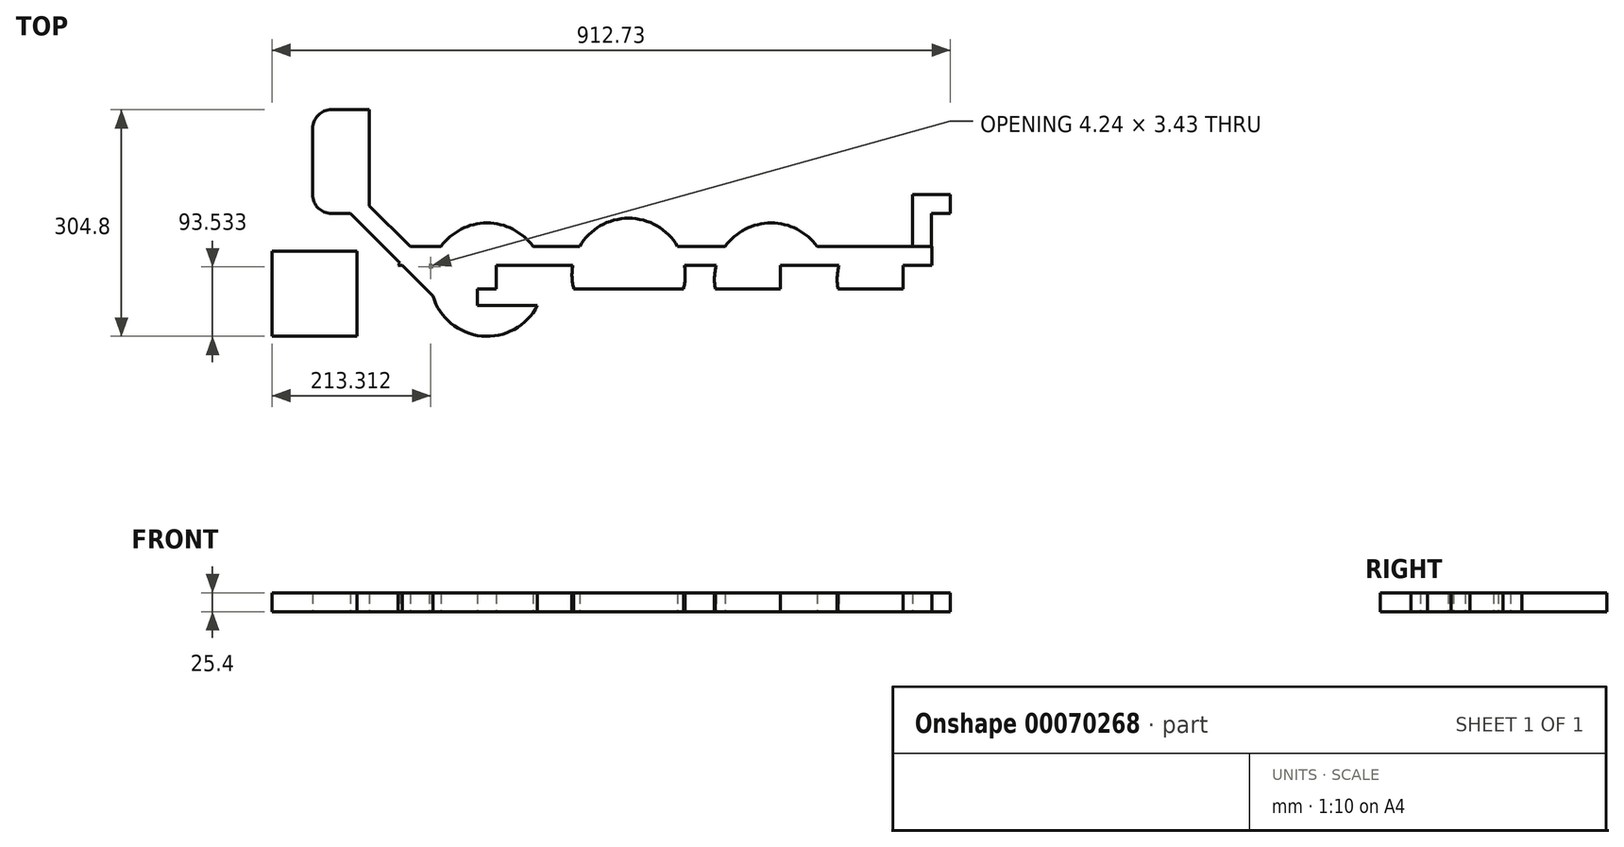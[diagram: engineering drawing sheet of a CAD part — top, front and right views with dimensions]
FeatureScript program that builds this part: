
annotation { "Feature Type Name" : "Feature", "Feature Type Description" : "" }
export const myFeature = defineFeature(function(context is Context, id is Id, definition is map)
    precondition{}
    {
        {
            var Q0;
            Q0=qCreatedBy(makeId("Top.planeOp"),FACE);
            var sketch = newSketch(context, id + "F0", { "sketchPlane" : qUnion([Q0])});
            skPoint(sketch, "E0", {"position": v(76.2, 76.2) * mm});
            skCircle(sketch, "E1", {"center": v(76.2, 76.2) * mm, "radius": 76.2 * mm});
            skLineSegment(sketch, "E2.left", {"start": v(63.5, 88.9) * mm, "end": v(63.5, 63.5) * mm});
            skLineSegment(sketch, "E2.right", {"start": v(88.9, 88.9) * mm, "end": v(88.9, 63.5) * mm});
            skLineSegment(sketch, "E2.top", {"start": v(63.5, 63.5) * mm, "end": v(88.9, 63.5) * mm});
            skLineSegment(sketch, "E2.bottom", {"start": v(63.5, 88.9) * mm, "end": v(88.9, 88.9) * mm});
            skLineSegment(sketch, "E3.left", {"start": v(610.82, 88.9) * mm, "end": v(610.82, 63.5) * mm});
            skPoint(sketch, "E4", {"position": v(458.42, 76.2) * mm});
            skLineSegment(sketch, "E3.bottom", {"start": v(610.82, 88.9) * mm, "end": v(636.22, 88.9) * mm});
            skCircle(sketch, "E5", {"center": v(458.42, 76.2) * mm, "radius": 76.2 * mm});
            skLineSegment(sketch, "E3.top", {"start": v(610.82, 63.5) * mm, "end": v(636.22, 63.5) * mm});
            skLineSegment(sketch, "E3.right", {"start": v(636.22, 88.9) * mm, "end": v(636.22, 63.5) * mm});
            skLineSegment(sketch, "E6", {"start": v(63.5, 88.9) * mm, "end": v(63.5, 95.25) * mm});
            skLineSegment(sketch, "E7", {"start": v(63.5, 95.25) * mm, "end": v(88.9, 95.25) * mm});
            skLineSegment(sketch, "E8", {"start": v(88.9, 95.25) * mm, "end": v(88.9, 88.9) * mm});
            skCircle(sketch, "E9", {"center": v(266.7, 82.55) * mm, "radius": 76.2 * mm});
            skLineSegment(sketch, "E10.left", {"start": v(254, 95.25) * mm, "end": v(254, 69.85) * mm});
            skLineSegment(sketch, "E10.right", {"start": v(279.4, 95.25) * mm, "end": v(279.4, 69.85) * mm});
            skLineSegment(sketch, "E10.top", {"start": v(254, 69.85) * mm, "end": v(279.4, 69.85) * mm});
            skLineSegment(sketch, "E10.bottom", {"start": v(254, 95.25) * mm, "end": v(279.4, 95.25) * mm});
            skCircle(sketch, "E11", {"center": v(623.52, 76.2) * mm, "radius": 76.2 * mm});
            skLineSegment(sketch, "E12.left", {"start": v(445.72, 88.9) * mm, "end": v(445.72, 63.5) * mm});
            skLineSegment(sketch, "E12.right", {"start": v(471.12, 88.9) * mm, "end": v(471.12, 63.5) * mm});
            skLineSegment(sketch, "E13", {"start": v(445.72, 88.9) * mm, "end": v(445.72, 95.25) * mm});
            skLineSegment(sketch, "E14", {"start": v(445.72, 95.25) * mm, "end": v(471.12, 95.25) * mm});
            skLineSegment(sketch, "E15", {"start": v(471.12, 95.25) * mm, "end": v(471.12, 88.9) * mm});
            skLineSegment(sketch, "E12.top", {"start": v(445.72, 63.5) * mm, "end": v(471.12, 63.5) * mm});
            skLineSegment(sketch, "E12.bottom", {"start": v(445.72, 88.9) * mm, "end": v(471.12, 88.9) * mm});
            skLineSegment(sketch, "E16.bottom", {"start": v(-98.71, 0) * mm, "end": v(-213.01, 0) * mm});
            skLineSegment(sketch, "E16.top", {"start": v(-98.71, 114.3) * mm, "end": v(-213.01, 114.3) * mm});
            skLineSegment(sketch, "E16.left", {"start": v(-98.71, 0) * mm, "end": v(-98.71, 114.3) * mm});
            skLineSegment(sketch, "E16.right", {"start": v(-213.01, 0) * mm, "end": v(-213.01, 114.3) * mm});
            skLineSegment(sketch, "E17", {"start": v(-107.59, 165.1) * mm, "end": v(3.22, 54.3) * mm});
            skLineSegment(sketch, "E18.bottom", {"start": v(-27.22, 120.65) * mm, "end": v(674.6, 120.65) * mm});
            skLineSegment(sketch, "E18.top", {"start": v(-43.2, 95.25) * mm, "end": v(674.6, 95.25) * mm});
            skLineSegment(sketch, "E18.right", {"start": v(674.6, 120.65) * mm, "end": v(674.6, 95.25) * mm});
            skLineSegment(sketch, "E19", {"start": v(-38.34, 131.77) * mm, "end": v(-60.65, 154.08) * mm});
            skLineSegment(sketch, "E20", {"start": v(-40.53, 133.96) * mm, "end": v(-27.22, 120.65) * mm});
            skLineSegment(sketch, "E21", {"start": v(-43.2, 95.25) * mm, "end": v(-27.22, 120.65) * mm});
            skLineSegment(sketch, "E22", {"start": v(699.72, 0) * mm, "end": v(699.72, 380) * mm, "construction": true});
            skLineSegment(sketch, "E23", {"start": v(636.22, 88.9) * mm, "end": v(636.22, 95.25) * mm});
            skLineSegment(sketch, "E24", {"start": v(636.22, 95.25) * mm, "end": v(610.82, 95.25) * mm});
            skLineSegment(sketch, "E25", {"start": v(610.82, 95.25) * mm, "end": v(610.82, 88.9) * mm});
            skLineSegment(sketch, "E26.bottom", {"start": v(674.32, 190.5) * mm, "end": v(699.72, 190.5) * mm});
            skLineSegment(sketch, "E26.top", {"start": v(674.32, 165.1) * mm, "end": v(699.72, 165.1) * mm});
            skLineSegment(sketch, "E26.left", {"start": v(674.32, 190.5) * mm, "end": v(674.32, 165.1) * mm});
            skLineSegment(sketch, "E26.right", {"start": v(699.72, 190.5) * mm, "end": v(699.72, 165.1) * mm});
            skLineSegment(sketch, "E27.bottom", {"start": v(674.32, 190.5) * mm, "end": v(648.92, 190.5) * mm});
            skLineSegment(sketch, "E27.top", {"start": v(674.32, 120.94) * mm, "end": v(648.92, 120.94) * mm});
            skLineSegment(sketch, "E27.left", {"start": v(674.32, 190.5) * mm, "end": v(674.32, 120.94) * mm});
            skLineSegment(sketch, "E27.right", {"start": v(648.92, 190.5) * mm, "end": v(648.92, 120.94) * mm});
            skLineSegment(sketch, "E28", {"start": v(-9.08, 102.51) * mm, "end": v(1.62, 91.82) * mm});
            skLineSegment(sketch, "E29", {"start": v(0, 0) * mm, "end": v(699.72, 0) * mm, "construction": true});
            skLineSegment(sketch, "E30", {"start": v(-107.59, 165.1) * mm, "end": v(-107.59, 304.8) * mm});
            skLineSegment(sketch, "E31", {"start": v(699.72, 165.1) * mm, "end": v(699.72, 304.8) * mm});
            skLineSegment(sketch, "E32", {"start": v(-107.59, 304.8) * mm, "end": v(699.72, 304.8) * mm, "construction": true});
            skLineSegment(sketch, "E33", {"start": v(940.54, 165.1) * mm, "end": v(-132.99, 165.1) * mm, "construction": true});
            skLineSegment(sketch, "E34", {"start": v(-54.83, 148.26) * mm, "end": v(-71.67, 165.1) * mm});
            skLineSegment(sketch, "E35.bottom", {"start": v(-107.59, 304.8) * mm, "end": v(-82.19, 304.8) * mm});
            skLineSegment(sketch, "E35.left", {"start": v(-107.59, 304.8) * mm, "end": v(-107.59, 165.1) * mm});
            skLineSegment(sketch, "E35.right", {"start": v(-82.19, 304.8) * mm, "end": v(-82.19, 175.62) * mm});
            skLineSegment(sketch, "E36", {"start": v(-71.67, 165.1) * mm, "end": v(-82.19, 175.62) * mm});
            skLineSegment(sketch, "E37.bottom", {"start": v(-107.59, 304.8) * mm, "end": v(-132.99, 304.8) * mm});
            skLineSegment(sketch, "E37.top", {"start": v(-107.59, 165.1) * mm, "end": v(-132.99, 165.1) * mm});
            skLineSegment(sketch, "E37.right", {"start": v(-158.39, 279.4) * mm, "end": v(-158.39, 190.5) * mm});
            skArc(sketch, "E38", {"start": v(-158.39, 279.4) * mm, "mid": v(-150.95, 297.36) * mm, "end": v(-132.99, 304.8) * mm});
            skPoint(sketch, "E38.centerSnap0", {"position": v(-132.99, 304.8) * mm});
            skPoint(sketch, "E39.orphan", {"position": v(-158.39, 304.8) * mm});
            skArc(sketch, "E40", {"start": v(-158.39, 190.5) * mm, "mid": v(-150.95, 172.54) * mm, "end": v(-132.99, 165.1) * mm});
            skPoint(sketch, "E40.centerSnap0", {"position": v(-132.99, 165.1) * mm});
            skPoint(sketch, "E41.orphan", {"position": v(-158.39, 165.1) * mm});
            skLineSegment(sketch, "E42.trimOffspring", {"start": v(-158.39, 165.1) * mm, "end": v(-974.91, 165.1) * mm, "construction": true});
            skLineSegment(sketch, "E43", {"start": v(-9.2, 66.72) * mm, "end": v(40.64, 16.87) * mm, "construction": true});
            skLineSegment(sketch, "E44.bottom", {"start": v(63.5, 63.5) * mm, "end": v(676.08, 63.5) * mm});
            skLineSegment(sketch, "E44.top", {"start": v(63.5, 41.23) * mm, "end": v(676.08, 41.23) * mm});
            skLineSegment(sketch, "E44.left", {"start": v(63.5, 63.5) * mm, "end": v(63.5, 41.23) * mm});
            skLineSegment(sketch, "E44.right", {"start": v(676.08, 63.5) * mm, "end": v(676.08, 41.23) * mm});
            skSolve(sketch);
        }
        {
            var Q0;
            Q0=makeQuery(id+"F0.imprint","IMPRINT",FACE,{"disambiguationData":[TD([[makeQuery(id+"F0.imprint","IMPRINT",EDGE,{"derivedFrom":sQuery(id+"F0.wireOp",EDGE,"E16.bottom")}),-1.0]])]});
            var Q1;
            Q1=makeQuery(id+"F0.imprint","IMPRINT",FACE,{"disambiguationData":[TD([[makeQuery(id+"F0.imprint","IMPRINT",EDGE,{"derivedFrom":sQuery(id+"F0.wireOp",EDGE,"E3.left")}),-1.0]])]});
            var Q2;
            Q2=makeQuery(id+"F0.imprint","IMPRINT",FACE,{"disambiguationData":[TD([[makeQuery(id+"F0.imprint","IMPRINT",EDGE,{"derivedFrom":sQuery(id+"F0.wireOp",EDGE,"E12.left")}),-1.0]])]});
            var Q3;
            Q3=makeQuery(id+"F0.imprint","IMPRINT",FACE,{"disambiguationData":[TD([[makeQuery(id+"F0.imprint","IMPRINT",EDGE,{"derivedFrom":sQuery(id+"F0.wireOp",EDGE,"E2.left")}),-1.0]])]});
            var Q4;
            {var subQ6=sQuery(id+"F0.wireOp",EDGE,"E19");Q4=makeQuery(id+"F0.imprint","IMPRINT",FACE,{"disambiguationData":[TD([[makeQuery(id+"F0.imprint","IMPRINT",EDGE,{"derivedFrom":subQ6}),1.0]])]});}
            var Q5;
            {var subQ2=sQuery(id+"F0.wireOp",EDGE,"E9");var subQ4=sQuery(id+"F0.wireOp",EDGE,"E18.bottom");var subQ5=makeQuery(id+"F0.imprint","INTERSECT",VERTEX,{"disambiguationData":[OD(0.0)],"derivedFrom":[subQ2,subQ4]});Q5=makeQuery(id+"F0.imprint","IMPRINT",FACE,{"disambiguationData":[TD([[makeQuery(id+"F0.imprint","IMPRINT",EDGE,{"disambiguationData":[TD([[subQ5,1.0]])],"derivedFrom":subQ2}),1.0]])]});}
            var Q6;
            {var subQ0=sQuery(id+"F0.wireOp",EDGE,"E18.right");Q6=makeQuery(id+"F0.imprint","IMPRINT",FACE,{"disambiguationData":[TD([[makeQuery(id+"F0.imprint","IMPRINT",EDGE,{"derivedFrom":subQ0}),-1.0]])]});}
            var Q7;
            {var subQ1=sQuery(id+"F0.wireOp",EDGE,"E10.left");Q7=makeQuery(id+"F0.imprint","IMPRINT",FACE,{"disambiguationData":[TD([[makeQuery(id+"F0.imprint","IMPRINT",EDGE,{"derivedFrom":subQ1}),-1.0]])]});}
            var Q8;
            {var subQ0=sQuery(id+"F0.wireOp",EDGE,"E18.bottom");var subQ1=sQuery(id+"F0.wireOp",EDGE,"E5");var subQ2=makeQuery(id+"F0.imprint","INTERSECT",VERTEX,{"disambiguationData":[OD(1.0)],"derivedFrom":[subQ1,subQ0]});Q8=makeQuery(id+"F0.imprint","IMPRINT",FACE,{"disambiguationData":[TD([[makeQuery(id+"F0.imprint","IMPRINT",EDGE,{"disambiguationData":[TD([[subQ2,-1.0]])],"derivedFrom":subQ1}),-1.0]])]});}
            var Q9;
            {var subQ0=sQuery(id+"F0.wireOp",EDGE,"E18.bottom");var subQ1=sQuery(id+"F0.wireOp",EDGE,"E5");var subQ2=makeQuery(id+"F0.imprint","INTERSECT",VERTEX,{"disambiguationData":[OD(0.0)],"derivedFrom":[subQ1,subQ0]});Q9=makeQuery(id+"F0.imprint","IMPRINT",FACE,{"disambiguationData":[TD([[makeQuery(id+"F0.imprint","IMPRINT",EDGE,{"disambiguationData":[TD([[subQ2,1.0]])],"derivedFrom":subQ1}),-1.0]])]});}
            var Q10;
            Q10=makeQuery(id+"F0.imprint","IMPRINT",FACE,{"disambiguationData":[TD([[makeQuery(id+"F0.imprint","IMPRINT",EDGE,{"derivedFrom":sQuery(id+"F0.wireOp",EDGE,"E37.bottom")}),1.0]])]});
            var Q11;
            {var subQ0=sQuery(id+"F0.wireOp",EDGE,"E18.bottom");var subQ1=sQuery(id+"F0.wireOp",EDGE,"E1");var subQ2=makeQuery(id+"F0.imprint","INTERSECT",VERTEX,{"disambiguationData":[OD(0.0)],"derivedFrom":[subQ1,subQ0]});Q11=makeQuery(id+"F0.imprint","IMPRINT",FACE,{"disambiguationData":[TD([[makeQuery(id+"F0.imprint","IMPRINT",EDGE,{"disambiguationData":[TD([[subQ2,1.0]])],"derivedFrom":subQ1}),-1.0]])]});}
            var Q12;
            {var subQ0=sQuery(id+"F0.wireOp",EDGE,"E18.bottom");var subQ1=sQuery(id+"F0.wireOp",EDGE,"E1");var subQ2=makeQuery(id+"F0.imprint","INTERSECT",VERTEX,{"disambiguationData":[OD(0.0)],"derivedFrom":[subQ1,subQ0]});Q12=makeQuery(id+"F0.imprint","IMPRINT",FACE,{"disambiguationData":[TD([[makeQuery(id+"F0.imprint","IMPRINT",EDGE,{"disambiguationData":[TD([[subQ2,1.0]])],"derivedFrom":subQ1}),1.0]])]});}
            var Q13;
            {var subQ0=sQuery(id+"F0.wireOp",EDGE,"E18.bottom");var subQ1=sQuery(id+"F0.wireOp",EDGE,"E9");var subQ2=makeQuery(id+"F0.imprint","INTERSECT",VERTEX,{"disambiguationData":[OD(0.0)],"derivedFrom":[subQ1,subQ0]});Q13=makeQuery(id+"F0.imprint","IMPRINT",FACE,{"disambiguationData":[TD([[makeQuery(id+"F0.imprint","IMPRINT",EDGE,{"disambiguationData":[TD([[subQ2,-1.0]])],"derivedFrom":subQ1}),1.0]])]});}
            var Q14;
            {var subQ0=sQuery(id+"F0.wireOp",EDGE,"E18.bottom");var subQ1=sQuery(id+"F0.wireOp",EDGE,"E5");var subQ2=makeQuery(id+"F0.imprint","INTERSECT",VERTEX,{"disambiguationData":[OD(0.0)],"derivedFrom":[subQ1,subQ0]});Q14=makeQuery(id+"F0.imprint","IMPRINT",FACE,{"disambiguationData":[TD([[makeQuery(id+"F0.imprint","IMPRINT",EDGE,{"disambiguationData":[TD([[subQ2,-1.0]])],"derivedFrom":subQ1}),1.0]])]});}
            var Q15;
            {var subQ0=sQuery(id+"F0.wireOp",EDGE,"E18.bottom");var subQ1=sQuery(id+"F0.wireOp",EDGE,"E1");var subQ2=makeQuery(id+"F0.imprint","INTERSECT",VERTEX,{"disambiguationData":[OD(0.0)],"derivedFrom":[subQ1,subQ0]});Q15=makeQuery(id+"F0.imprint","IMPRINT",FACE,{"disambiguationData":[TD([[makeQuery(id+"F0.imprint","IMPRINT",EDGE,{"disambiguationData":[TD([[subQ2,-1.0]])],"derivedFrom":subQ1}),1.0]])]});}
            var Q16;
            {var subQ2=sQuery(id+"F0.wireOp",EDGE,"E5");var subQ4=sQuery(id+"F0.wireOp",EDGE,"E18.bottom");var subQ6=makeQuery(id+"F0.imprint","INTERSECT",VERTEX,{"disambiguationData":[OD(0.0)],"derivedFrom":[subQ2,subQ4]});Q16=makeQuery(id+"F0.imprint","IMPRINT",FACE,{"disambiguationData":[TD([[makeQuery(id+"F0.imprint","IMPRINT",EDGE,{"disambiguationData":[TD([[subQ6,1.0]])],"derivedFrom":subQ2}),1.0]])]});}
            var Q17;
            {var subQ6=sQuery(id+"F0.wireOp",EDGE,"E27.bottom");Q17=makeQuery(id+"F0.imprint","IMPRINT",FACE,{"disambiguationData":[TD([[makeQuery(id+"F0.imprint","IMPRINT",EDGE,{"derivedFrom":subQ6}),1.0]])]});}
            var Q18;
            {var subQ1=sQuery(id+"F0.wireOp",EDGE,"E18.bottom");var subQ3=sQuery(id+"F0.wireOp",EDGE,"E1");var subQ4=makeQuery(id+"F0.imprint","INTERSECT",VERTEX,{"disambiguationData":[OD(1.0)],"derivedFrom":[subQ3,subQ1]});Q18=makeQuery(id+"F0.imprint","IMPRINT",FACE,{"disambiguationData":[TD([[makeQuery(id+"F0.imprint","IMPRINT",EDGE,{"disambiguationData":[TD([[subQ4,-1.0]])],"derivedFrom":subQ3}),-1.0]])]});}
            var Q19;
            {var subQ0=sQuery(id+"F0.wireOp",EDGE,"E17");var subQ1=sQuery(id+"F0.wireOp",EDGE,"E1");var subQ2=makeQuery(id+"F0.imprint","INTERSECT",VERTEX,{"derivedFrom":[subQ1,subQ0]});Q19=makeQuery(id+"F0.imprint","IMPRINT",FACE,{"disambiguationData":[TD([[makeQuery(id+"F0.imprint","IMPRINT",EDGE,{"disambiguationData":[TD([[subQ2,1.0]])],"derivedFrom":subQ1}),-1.0]])]});}
            var Q20;
            {var subQ5=sQuery(id+"F0.wireOp",EDGE,"E27.top");Q20=makeQuery(id+"F0.imprint","IMPRINT",FACE,{"disambiguationData":[TD([[makeQuery(id+"F0.imprint","IMPRINT",EDGE,{"derivedFrom":subQ5}),-1.0]])]});}
            var Q21;
            {var subQ0=sQuery(id+"F0.wireOp",EDGE,"E21");var subQ1=sQuery(id+"F0.wireOp",EDGE,"E17");var subQ2=makeQuery(id+"F0.imprint","INTERSECT",VERTEX,{"derivedFrom":[subQ1,subQ0]});Q21=makeQuery(id+"F0.imprint","IMPRINT",FACE,{"disambiguationData":[TD([[makeQuery(id+"F0.imprint","IMPRINT",EDGE,{"disambiguationData":[TD([[subQ2,-1.0]])],"derivedFrom":subQ1}),-1.0]])]});}
            var Q22;
            {var subQ0=sQuery(id+"F0.wireOp",EDGE,"E10.left");Q22=makeQuery(id+"F0.imprint","IMPRINT",FACE,{"disambiguationData":[TD([[makeQuery(id+"F0.imprint","IMPRINT",EDGE,{"derivedFrom":subQ0}),1.0]])]});}
            var Q23;
            Q23=makeQuery(id+"F0.imprint","IMPRINT",FACE,{"disambiguationData":[TD([[makeQuery(id+"F0.imprint","IMPRINT",EDGE,{"derivedFrom":sQuery(id+"F0.wireOp",EDGE,"E2.left")}),1.0]])]});
            var Q24;
            {var subQ0=sQuery(id+"F0.wireOp",EDGE,"E26.bottom");Q24=makeQuery(id+"F0.imprint","IMPRINT",FACE,{"disambiguationData":[TD([[makeQuery(id+"F0.imprint","IMPRINT",EDGE,{"derivedFrom":subQ0}),-1.0]])]});}
            var Q25;
            Q25=makeQuery(id+"F0.imprint","IMPRINT",FACE,{"disambiguationData":[TD([[makeQuery(id+"F0.imprint","IMPRINT",EDGE,{"derivedFrom":sQuery(id+"F0.wireOp",EDGE,"E12.left")}),1.0]])]});
            var Q26;
            {var subQ0=sQuery(id+"F0.wireOp",EDGE,"E13");Q26=makeQuery(id+"F0.imprint","IMPRINT",FACE,{"disambiguationData":[TD([[makeQuery(id+"F0.imprint","IMPRINT",EDGE,{"derivedFrom":subQ0}),-1.0]])]});}
            var Q27;
            Q27=makeQuery(id+"F0.imprint","IMPRINT",FACE,{"disambiguationData":[TD([[makeQuery(id+"F0.imprint","IMPRINT",EDGE,{"derivedFrom":sQuery(id+"F0.wireOp",EDGE,"E3.left")}),1.0]])]});
            var Q28;
            Q28=makeQuery(id+"F0.imprint","IMPRINT",FACE,{"disambiguationData":[TD([[makeQuery(id+"F0.imprint","IMPRINT",EDGE,{"derivedFrom":sQuery(id+"F0.wireOp",EDGE,"E2.bottom")}),1.0]])]});
            var Q29;
            Q29=makeQuery(id+"F0.imprint","IMPRINT",FACE,{"disambiguationData":[TD([[makeQuery(id+"F0.imprint","IMPRINT",EDGE,{"derivedFrom":sQuery(id+"F0.wireOp",EDGE,"E3.bottom")}),1.0]])]});
            extrude(context, id + "F1", {"entities" : qUnion([Q0, Q1, Q2, Q3, Q4, Q5, Q6, Q7, Q8, Q9, Q10, Q11, Q12, Q13, Q14, Q15, Q16, Q17, Q18, Q19, Q20, Q21, Q22, Q23, Q24, Q25, Q26, Q27, Q28, Q29]), "depth" : 25.4 * mm});
        }
    });
